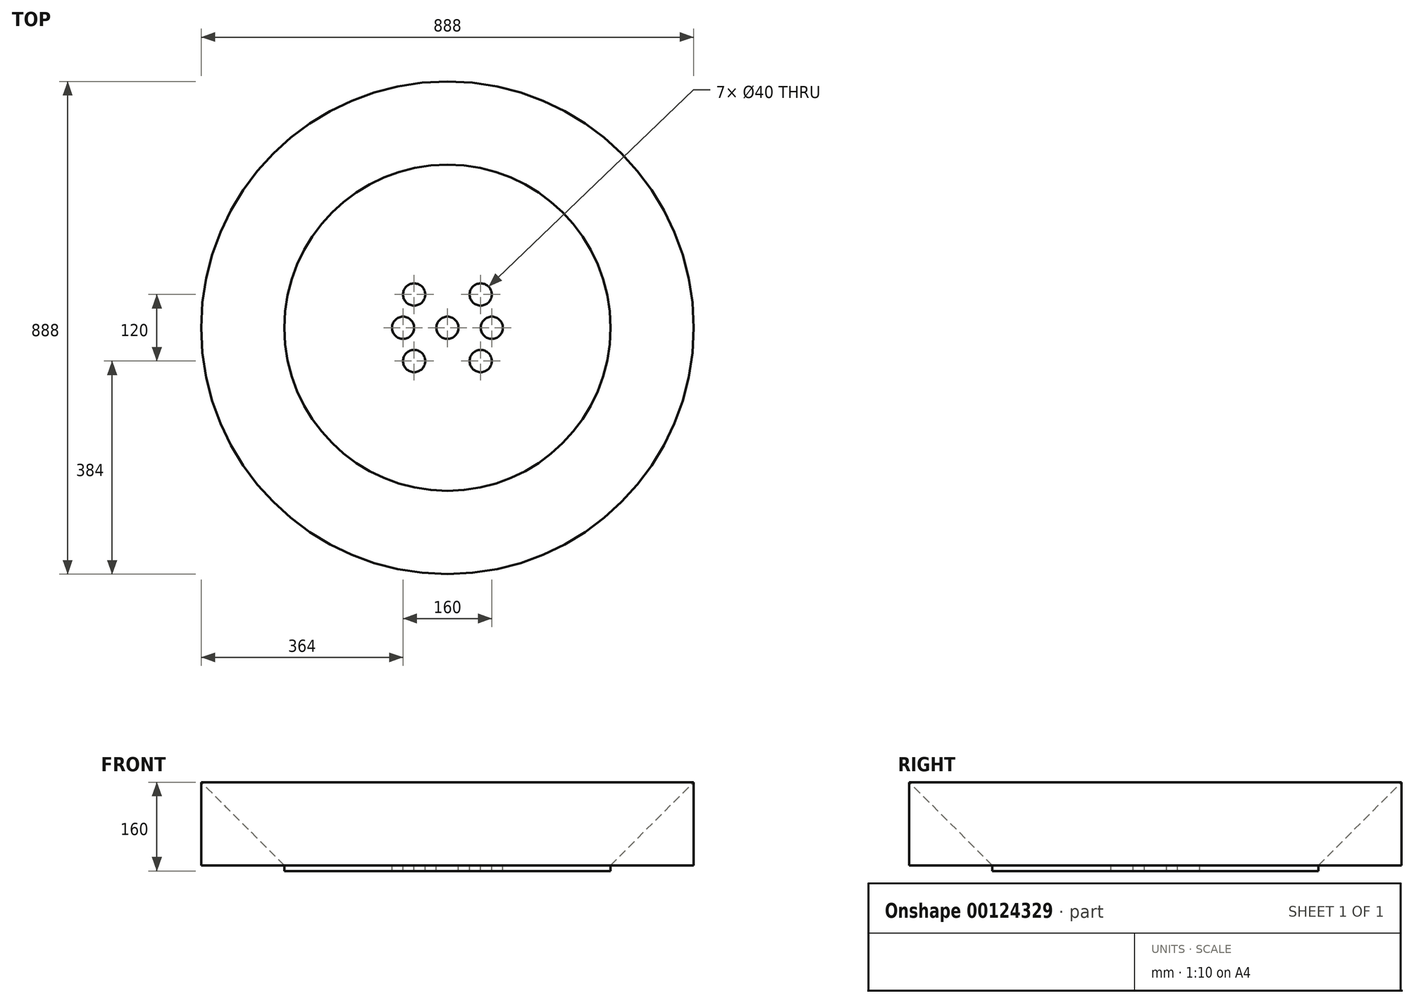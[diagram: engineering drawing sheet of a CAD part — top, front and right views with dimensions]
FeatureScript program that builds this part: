
annotation { "Feature Type Name" : "Feature", "Feature Type Description" : "" }
export const myFeature = defineFeature(function(context is Context, id is Id, definition is map)
    precondition{}
    {
        {
            var Q0;
            Q0=qCreatedBy(makeId("Front.planeOp"),FACE);
            var sketch = newSketch(context, id + "F0", { "sketchPlane" : qUnion([Q0])});
            skLineSegment(sketch, "E0", {"start": v(0, 0) * mm, "end": v(444, 0) * mm, "construction": true});
            skLineSegment(sketch, "E1", {"start": v(0, 0) * mm, "end": v(-444, 0) * mm, "construction": true});
            skLineSegment(sketch, "E2", {"start": v(0, 0) * mm, "end": v(0, 150) * mm, "construction": true});
            skLineSegment(sketch, "E3", {"start": v(0, 150) * mm, "end": v(444, 150) * mm, "construction": true});
            skLineSegment(sketch, "E4", {"start": v(0, 150) * mm, "end": v(-444, 150) * mm, "construction": true});
            skLineSegment(sketch, "E5", {"start": v(-444, 150) * mm, "end": v(-444, 300) * mm});
            skLineSegment(sketch, "E6", {"start": v(-444, 300) * mm, "end": v(-294, 150) * mm});
            skLineSegment(sketch, "E7", {"start": v(-444, 150) * mm, "end": v(-294, 150) * mm});
            skLineSegment(sketch, "E8", {"start": v(0, 0) * mm, "end": v(0, 544.8) * mm});
            skSolve(sketch);
        }
        {
            var Q0;
            Q0=makeQuery(id+"F0.imprint","IMPRINT",FACE,{"disambiguationData":[TD([[makeQuery(id+"F0.imprint","IMPRINT",EDGE,{"derivedFrom":sQuery(id+"F0.wireOp",EDGE,"E5")}),-1.0]])]});
            var Q1;
            Q1=sQuery(id+"F0.wireOp",EDGE,"E8");
            revolve(context, id + "F1", {"entities" : qUnion([Q0]), "axis" : qUnion([Q1]), "revolveType" : RevolveType.FULL});
        }
        {
            var Q0;
            Q0=makeQuery(id+"F1.opRevolve","SWEPT_FACE",FACE,{"disambiguationData":[OSD([sQuery(id+"F0.wireOp",EDGE,"E7")])]});
            var sketch = newSketch(context, id + "F2", { "sketchPlane" : qUnion([Q0])});
            skLineSegment(sketch, "E9", {"start": v(0, 0) * mm, "end": v(0, 60) * mm, "construction": true});
            skLineSegment(sketch, "E10", {"start": v(0, -60) * mm, "end": v(0, 0) * mm, "construction": true});
            skLineSegment(sketch, "E11", {"start": v(0, 60) * mm, "end": v(60, 60) * mm, "construction": true});
            skLineSegment(sketch, "E12", {"start": v(0, -60) * mm, "end": v(60, -60) * mm, "construction": true});
            skLineSegment(sketch, "E13", {"start": v(0, 0) * mm, "end": v(80, 0) * mm});
            skLineSegment(sketch, "E14", {"start": v(60, -60) * mm, "end": v(80, 0) * mm, "construction": true});
            skLineSegment(sketch, "E15", {"start": v(80, 0) * mm, "end": v(60, 60) * mm, "construction": true});
            skLineSegment(sketch, "E16.MirrorCS", {"start": v(0, -60) * mm, "end": v(-60, -60) * mm, "construction": true});
            skLineSegment(sketch, "E17.MirrorCS", {"start": v(-60, -60) * mm, "end": v(-80, 0) * mm, "construction": true});
            skLineSegment(sketch, "E18.MirrorCS", {"start": v(0, 60) * mm, "end": v(-60, 60) * mm, "construction": true});
            skLineSegment(sketch, "E19.MirrorCS", {"start": v(-80, 0) * mm, "end": v(-60, 60) * mm, "construction": true});
            skLineSegment(sketch, "E20", {"start": v(60, -60) * mm, "end": v(60, 60) * mm});
            skLineSegment(sketch, "E21", {"start": v(-60, -60) * mm, "end": v(-60, 60) * mm});
            skLineSegment(sketch, "E22", {"start": v(-80, 0) * mm, "end": v(0, 0) * mm});
            skCircle(sketch, "E23", {"center": v(-60, 60) * mm, "radius": 20 * mm});
            skCircle(sketch, "E24", {"center": v(-80, 0) * mm, "radius": 20 * mm});
            skCircle(sketch, "E25", {"center": v(-60, -60) * mm, "radius": 20 * mm});
            skCircle(sketch, "E26", {"center": v(60, -60) * mm, "radius": 20 * mm});
            skCircle(sketch, "E27", {"center": v(80, 0) * mm, "radius": 20 * mm});
            skCircle(sketch, "E28", {"center": v(60, 60) * mm, "radius": 20 * mm});
            skCircle(sketch, "E29", {"center": v(0, 0) * mm, "radius": 20 * mm});
            skLineSegment(sketch, "E30", {"start": v(0, 0) * mm, "end": v(0, 155) * mm, "construction": true});
            skLineSegment(sketch, "E31", {"start": v(0, 155) * mm, "end": v(-249.82, 155) * mm});
            skLineSegment(sketch, "E32", {"start": v(0, -294) * mm, "end": v(-249.82, 155) * mm});
            skLineSegment(sketch, "E33", {"start": v(0, 155) * mm, "end": v(0, 125) * mm});
            skLineSegment(sketch, "E34", {"start": v(0, 125) * mm, "end": v(203.08, 125) * mm});
            skLineSegment(sketch, "E35", {"start": v(203.08, 125) * mm, "end": v(0, -240) * mm});
            skPoint(sketch, "E35.endSnap0", {"position": v(0, 140) * mm});
            skLineSegment(sketch, "E36", {"start": v(0, -240) * mm, "end": v(-203.08, 125) * mm});
            skLineSegment(sketch, "E37", {"start": v(-203.08, 125) * mm, "end": v(0, 125) * mm});
            skCircle(sketch, "E38", {"center": v(0, 0) * mm, "radius": 294 * mm});
            skLineSegment(sketch, "E39", {"start": v(0, 155) * mm, "end": v(249.82, 155) * mm});
            skLineSegment(sketch, "E40", {"start": v(249.82, 155) * mm, "end": v(0, -294) * mm});
            skSolve(sketch);
        }
        {
            var Q0;
            Q0=qCreatedBy(makeId("Top.planeOp"),FACE);
            var sketch = newSketch(context, id + "F3", { "sketchPlane" : qUnion([Q0])});
            skCircle(sketch, "E41", {"center": v(0, 0) * mm, "radius": 450 * mm});
            skCircle(sketch, "E42", {"center": v(0, 0) * mm, "radius": 445 * mm});
            skSolve(sketch);
        }
        {
            var Q0;
            Q0=sQuery(id+"F3.wireOp",EDGE,"E42");
            var Q1;
            Q1=sQuery(id+"F3.wireOp",EDGE,"E41");
            extrude(context, id + "F4", {"bodyType" : ToolBodyType.SURFACE, "surfaceEntities" : qUnion([Q0, Q1]), "depth" : 941 * mm});
        }
        {
            var Q0;
            {var subQ0=sQuery(id+"F2.wireOp",EDGE,"E32");Q0=makeQuery(id+"F2.imprint","IMPRINT",FACE,{"disambiguationData":[TD([[makeQuery(id+"F2.imprint","IMPRINT",EDGE,{"derivedFrom":subQ0}),1.0]])]});}
            var Q1;
            Q1=makeQuery(id+"F2.imprint","IMPRINT",FACE,{"disambiguationData":[TD([[makeQuery(id+"F2.imprint","IMPRINT",EDGE,{"derivedFrom":sQuery(id+"F2.wireOp",EDGE,"E23")}),-1.0]])]});
            var Q2;
            Q2=makeQuery(id+"F2.imprint","IMPRINT",FACE,{"disambiguationData":[TD([[makeQuery(id+"F2.imprint","IMPRINT",EDGE,{"derivedFrom":sQuery(id+"F2.wireOp",EDGE,"E31")}),1.0]])]});
            var Q3;
            {var subQ0=sQuery(id+"F2.wireOp",EDGE,"E31");Q3=makeQuery(id+"F2.imprint","IMPRINT",FACE,{"disambiguationData":[TD([[makeQuery(id+"F2.imprint","IMPRINT",EDGE,{"derivedFrom":subQ0}),-1.0]])]});}
            var Q4;
            {var subQ0=sQuery(id+"F2.wireOp",EDGE,"E40");Q4=makeQuery(id+"F2.imprint","IMPRINT",FACE,{"disambiguationData":[TD([[makeQuery(id+"F2.imprint","IMPRINT",EDGE,{"derivedFrom":subQ0}),1.0]])]});}
            extrude(context, id + "F5", {"entities" : qUnion([Q0, Q1, Q2, Q3, Q4]), "depth" : 10 * mm});
        }
    });
